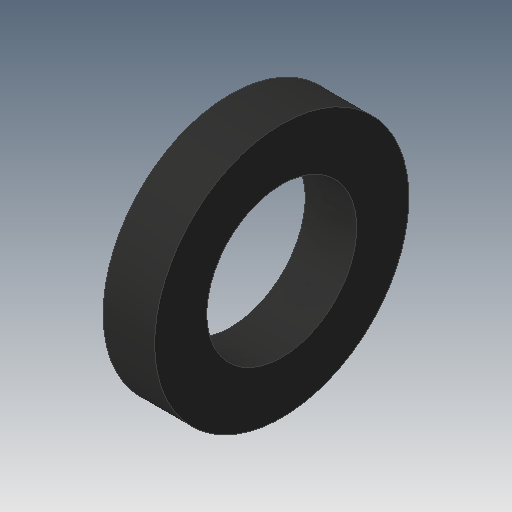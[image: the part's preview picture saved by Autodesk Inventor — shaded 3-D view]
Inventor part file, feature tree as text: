
AUTODESK INVENTOR PART (.ipt)
format: ipt  version: 2018 (Build 220112000, 112)  size: 93,184 bytes
history: native  units: in
note: dims shown in document units (in); Inventor stores cm internally (conversion verified against a paired STEP export)
features: other x3, sketch x1
ambient origin geometry x8: Origin, YZ Plane, XZ Plane, XY Plane, X Axis, Y Axis, Z Axis, Center Point
bodies: Solid1 (feature_tree)
feature tree (4):
  other  "Tire.ipt"
  other  "Solid1::Tire.ipt"
  other  "TaggingFeature1"
  sketch  "Sketch1"  dims[d0=0.3937in]
